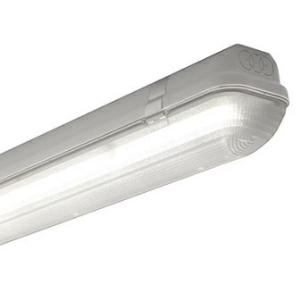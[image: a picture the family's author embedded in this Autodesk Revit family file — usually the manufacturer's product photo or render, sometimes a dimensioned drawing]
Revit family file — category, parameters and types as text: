
# Revit family: 3f_filippi_-_3f_linda_atex_3f_filippi_-_58472_-_3f_linda_led_1x24w_atex_3d_l1270
name_source: partatom
category: Lighting Fixtures
units: mm (PartAtom-declared; Revit-internal decimal feet)

## family parameters
Cut with Voids When Loaded = No
Host = Face
Light Source = No
Part Type = Normal
Room Calculation Point = No
Round Connector Dimension = Use Diameter
Shared = No

## types (1)
- 3F Filippi - 3F Linda ATEX (1 x LED, 4065 lm, 28 W, 4000 K)
    Apparent Load = 28 VA
    Approval mark = ENEC
    CIE Flux Codes = 44 77 94 97 100
    Color Rendering = 80
    Color Temperature = 4000 K
    Control Gear = Electronic ballast
    Default Elevation = 1800 mm
    Description = ILLUMINOTECHNICAL
Luminous efficiency 100% (DLOR 97%, ULOR 3%).
Initial luminous flux of the luminaire 4065 lm.
Controlled symmetric distribution.
Installation Interdistance Transv.D = 1.77 x hu - Long.D = 1.17 x hu.
Tabular UGR (CIE 117 - 4H-8H; S=0.25H; 70/50/20): RUG 22 - 22.9.
Beam angle: 109° - 64°.
Luminous efficacy 145 lm/W.
Lifetime (L93/B10): 30000 h. (tq+25°C)
Lifetime (L90/B10): 50000 h. (tq+25°C)
Lifetime (L85/B10): 80000 h. (tq+25°C)
Lifetime (L80/B10): 100000 h. (tq+25°C)
Lifetime (L85/B10): 50000 h. (tq+35°C)
Sudden decreased luminous flux after 50000 hours: 0% (C0).
Photobiological safety in compliance with IEC/TR 62778: RG0 risk exempt, (IEC 62471).
In compliance with IEC/EN 62722-2-1 - IEC/EN 62717 standards.

SOURCE
Linear LED module 24W/840.
Energy efficiency class (UE 2019/2020 - UE 2019/2015): D.
CIE 13.3 Colour rendering index: CRI >80 (R9 <50%).
IES TM-30 Fidelity Index: Rf = 84 Rg = 95.
CCT nominal colour temperature 4000 K.
Colour initial tolerance (MacAdam): SDCM 3.

MECHANICAL
Self-extinguishing V2 polycarbonate housing, injection moulded, RAL 7035 grey.
Ecologic anti-aging injected sealing gasket.
Diffuser in self-extinguishing V2 polycarbonate, photo-engraved interior, UV stabilised, injection moulded with smooth outer surface, tamper-proof opening.
Gear-holder reflector in hot-dip galvanised steel, painted with white polyester base.
Snug fit safety snap-lock clips for diffuser mounting in stainless steel, screwdriver opening.
Fixing brackets in stainless steel.
Possibility for technicians to access the interior of the luminaire.
Luminaire with limited surface temperature. - D - (EN 60598-2-24)
Dimensions: 1270x100 mm, height 100 mm. Weight 2.059 kg.
IP66 protection degree.
Mechanical strength to impacts IK10 (20 joule).
Glow-wire test resistance 850°C.

ELECTRICAL
Halogen Free electronic wiring 230V-50/60Hz, power factor 0.90, THD <25%, constant output current, SELV, class I, 1 driver.
Power of the luminaire 28 W.
CE - IEC 60598-1 - EN 60598-1.
SAFE FLICKER: PstLM=<1 and SVM=<0.4 (IEC TR 61547-1 and IEC TR 63158), to ensure a more comfortable and safe light.
Luminaire compliant with EN 60598-2-22 for power supply from a centralised emergency system CPSS (Central Power Supply System), not incorporated in the luminaire - high risk areas excluded. The default power and flux are 100% in AC and 100% in DC.
Ambient temperature from -20°C to +35°C.
Temperature class T6 max 85°C.
Entry for power-supply cable through ATEX M20x1,5mm polyamide cable gland, supplied.
Relative humidity UR: <85%.

INSTALLATION
Ceiling / Suspended / Wall.
All accessories dedicated to this product are available on the Catalog and on our website www.3F-Filippi.com.

APPLICATIONS
Environments with ATEX explosive atmosphere (Conformity 2014/34/UE, EN IEC 60079-0, EN 60079-31): Group II, Category 3D (Ex Tc IIIC T85°C Dc).
Suitable product for food production plants (HACCP), IFS (Food Version 6), BRC (GSFS Food Version 7).
Dry, dusty indoor environments, subject to occasional water splashes.
Virtually shatterproof polycarbonate compatibly with the fumes / atmospheres that compromise the elasticity of plastic materials.
Not suitable for installation on surfaces subject to important vibrations, exposed to weather conditions, on ropes or poles.
Suitable for illumination of public car parks and parking grounds referred to DIN 67528:2018-04.

WARNING
Fixture not suitable for cold stores with an ambient temperature <0°C and/or relative humidity >85%.
Luminaire designed for disposal/recycling at end-of-life.
Replaceable (LED only) light source by a professional. Replaceable control gear by a professional.
    Height = 100 mm  [stored 0.328084 ft]
    Lamp = 1 x LED
    Lamp Light Flux = 4065 lm
    Lamp Power = 28 W
    Lamp count = 1
    Length = 1270 mm
    Lifetime = 50000 h
    Luminous efficacy = 145 lm/W
    Manufacturer = 3F Filippi
    ModVariant = No
    Model = 3F Filippi - 58472 - 3F Linda LED 1x24W ATEX 3D L1270
    Mounting Place = Ceiling
    Mounting Type = Pendant
    Number of Poles = 1
    OnlyDefault = Yes
    Power Factor = 1
    Product Name = 3F Filippi - 3F Linda ATEX
    Product group = pendant luminaire
    ProductGroupID = 9
    Protection Class = Protection class I
    Protection Degree = IP 66
    RLX_Detail_Level = 1
    RLX_Emergency_Light_Flux = 0 lm
    RLX_Emergency_Type = 0
    RLX_Emergency_Type_DB = No
    RlxData = <blob elided: 69345 chars, md5=aeb7c58c>
    Socket = socket
    Standby Power = 0 W
    System Light Flux = 4065 lm
    System Power = 28 W
    Type Comments = Product without accessories
    Type Image = 3ffilippi_3f_linda_led_1x.jpg
    URL = http://relux.com
    VarID = ---
    Voltage = 0 V
    Weight = 0.00 kg
    Width = 100 mm  [stored 0.328084 ft]

note: [stored X ft] marks values corroborated as IEEE doubles in the binary element streams (Revit-internal decimal feet)

## geometry (parser evidence)
native form markers: Blend x4, Sweep x8
no freeform markers — native parametric forms only
